# Revit family: Detail-HST Top Hat-Steel & Tube-HST-Section_Temp_e5a19375-dc16-4c4b-8fc2-10be2444a1d1
name_source: partatom
category: Detail Items
revit_build: Autodesk Revit 2016 (Build: 20160314_0715(x64)
units: mm (PartAtom-declared; Revit-internal decimal feet)

## family parameters
OmniClass Number = 23.35.20.14.14
OmniClass Title = Roof Battens
Rotate with component = No
Shared = No

## types (1)
- 60 HST Tophat 0.75 BMT
    Assembly Code = B1020230
    CBICode = 3411
    CBIDescription = Structural steelwork
    Coil Performance = Gauge 0.75-1.15mm; G500(MPa); 275g/m² (Zinc)
    Description = Steel & Tube HST Tophat sections are an economical, lightweight, versatile and easy to use product for roof purlins, wall girts and floor joists.
    Design Instruction = All the design information should be cross referenced with the current Steel & Tube Tophat Design Capacity Tables.
    Design Standard = Steel & Tube’s HST Tophat profiles are designed in accordance with AS/NZS 4600:2005
    Height_ANZRS = 60 mm  [stored 0.19685 ft]
    Manufacturer = Steel & Tube
    ManufacturerName = Steel & Tube
    ManufacturerURL = http://www.steelandtube.co.nz
    Material Standard = Steel & Tube’s HST Tophat profiles are manufactured from materials conforming to AS1397:2011
    Model = 60 HST Tophat 0.75 BMT
    ModifiedIssue_ANZRS = 20160526 $
    Profile = 0
    Profile70 = Yes
    Profile71 = No
    Profile72 = No
    Profile73 = No
    Profile74 = No
    Profile75 = No
    Profile76 = No
    SpecificationDescription = Steel & Tube Purlins & Girts
    SpecificationReference = 3411ST
    URL = http://www.steelandtube.co.nz
    Uniclass2015Code = Pr_20_76_51_21
    Uniclass2015Title = Cold-formed galvanized steel sections
    Uniclass2015Version = 2015
    Width_ANZRS = 108 mm  [stored 0.354331 ft]

note: [stored X ft] marks values corroborated as IEEE doubles in the binary element streams (Revit-internal decimal feet)

## geometry (parser evidence)
native form markers: Sweep x1
no freeform markers — native parametric forms only
